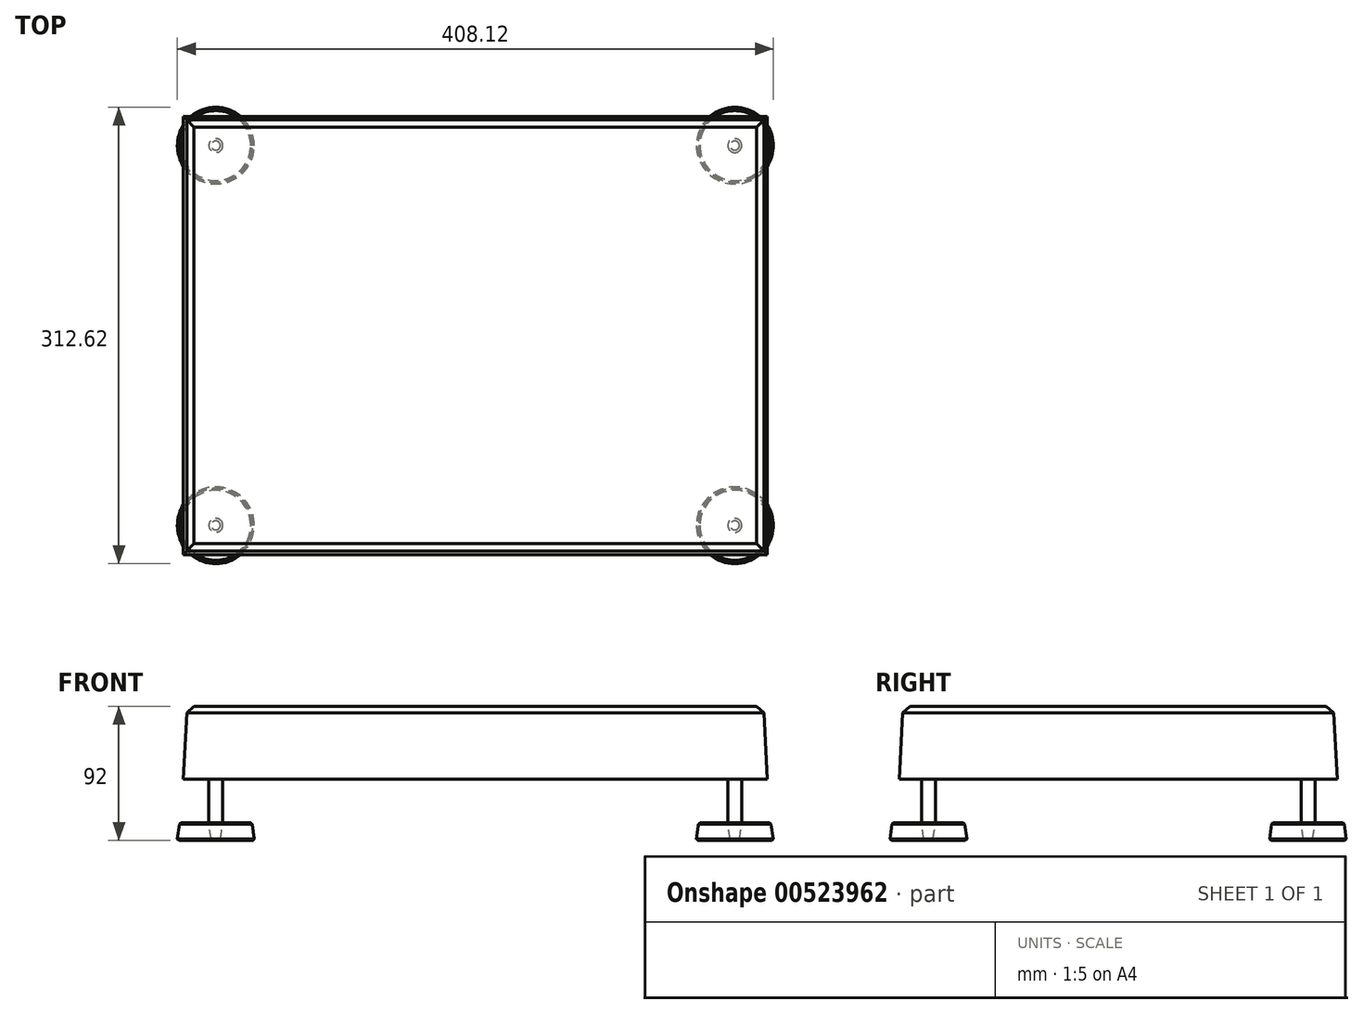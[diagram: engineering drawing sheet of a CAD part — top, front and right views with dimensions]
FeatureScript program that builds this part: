
annotation { "Feature Type Name" : "Feature", "Feature Type Description" : "" }
export const myFeature = defineFeature(function(context is Context, id is Id, definition is map)
    precondition{}
    {
        {
            var Q0;
            Q0=qCreatedBy(makeId("Top.planeOp"),FACE);
            var sketch = newSketch(context, id + "F0", { "sketchPlane" : qUnion([Q0])});
            skLineSegment(sketch, "E0.bottom", {"start": v(200, -150) * mm, "end": v(-200, -150) * mm});
            skLineSegment(sketch, "E0.top", {"start": v(200, 150) * mm, "end": v(-200, 150) * mm});
            skLineSegment(sketch, "E0.left", {"start": v(200, -150) * mm, "end": v(200, 150) * mm});
            skLineSegment(sketch, "E0.right", {"start": v(-200, -150) * mm, "end": v(-200, 150) * mm});
            skPoint(sketch, "E0.middle", {"position": v(0, 0) * mm});
            skSolve(sketch);
        }
        {
            var Q0;
            Q0=makeQuery(id+"F0.imprint","IMPRINT",FACE,{"disambiguationData":[TD([[makeQuery(id+"F0.imprint","IMPRINT",EDGE,{"derivedFrom":sQuery(id+"F0.wireOp",EDGE,"E0.bottom")}),-1.0]])]});
            extrude(context, id + "F1", {"entities" : qUnion([Q0]), "depth" : 50 * mm, "offsetDistance" : 25 * mm, "hasDraft" : true, "draftAngle" : 3 * degree, "draftPullDirection" : true});
        }
        {
            var Q0;
            Q0=makeQuery(id+"F1.opExtrude","CAP_EDGE",EDGE,{"disambiguationData":[OSD([sQuery(id+"F0.wireOp",EDGE,"E0.bottom")])],"isStart":false});
            var Q1;
            Q1=makeQuery(id+"F1.opExtrude","CAP_EDGE",EDGE,{"disambiguationData":[OSD([sQuery(id+"F0.wireOp",EDGE,"E0.right")])],"isStart":false});
            var Q2;
            Q2=makeQuery(id+"F1.opExtrude","CAP_EDGE",EDGE,{"disambiguationData":[OSD([sQuery(id+"F0.wireOp",EDGE,"E0.left")])],"isStart":false});
            var Q3;
            Q3=makeQuery(id+"F1.opExtrude","SWEPT_EDGE",EDGE,{"disambiguationData":[OSD([sQuery(id+"F0.wireOp",EDGE,"E0.bottom"),sQuery(id+"F0.wireOp",EDGE,"E0.left")])]});
            var Q4;
            Q4=makeQuery(id+"F1.opExtrude","CAP_EDGE",EDGE,{"disambiguationData":[OSD([sQuery(id+"F0.wireOp",EDGE,"E0.top")])],"isStart":false});
            var Q5;
            Q5=makeQuery(id+"F1.opExtrude","SWEPT_EDGE",EDGE,{"disambiguationData":[OSD([sQuery(id+"F0.wireOp",EDGE,"E0.top"),sQuery(id+"F0.wireOp",EDGE,"E0.right")])]});
            chamfer(context, id + "F2", {"entities" : qUnion([Q0, Q1, Q2, Q3, Q4, Q5]), "width" : 5 * mm, "tangentPropagation" : true});
        }
        {
            var Q0;
            Q0=makeQuery(id+"F1.opExtrude","CAP_FACE",FACE,{"disambiguationData":[OSD([sQuery(id+"F0.wireOp",EDGE,"E0.bottom"),sQuery(id+"F0.wireOp",EDGE,"E0.top"),sQuery(id+"F0.wireOp",EDGE,"E0.left"),sQuery(id+"F0.wireOp",EDGE,"E0.right")])],"isStart":true});
            var sketch = newSketch(context, id + "F3", { "sketchPlane" : qUnion([Q0])});
            skLineSegment(sketch, "E1", {"start": v(0, 0) * mm, "end": v(200, 0) * mm, "construction": true});
            skLineSegment(sketch, "E2", {"start": v(-2.63, 150) * mm, "end": v(0, 0) * mm, "construction": true});
            skCircle(sketch, "E3", {"center": v(177.75, 130) * mm, "radius": 4.79 * mm});
            skSolve(sketch);
        }
        {
            var Q0;
            Q0 = qSketchRegion(id + "F3", true);
            extrude(context, id + "F4", {"entities" : qUnion([Q0]), "depth" : 30 * mm, "offsetDistance" : 25 * mm});
        }
        {
            var Q0;
            Q0=makeQuery(id+"F4.opExtrude","CAP_FACE",FACE,{"disambiguationData":[OSD([sQuery(id+"F3.wireOp",EDGE,"E3")])],"isStart":false});
            var sketch = newSketch(context, id + "F5", { "sketchPlane" : qUnion([Q0])});
            skCircle(sketch, "E4.0.0", {"center": v(177.75, 130) * mm, "radius": 4.79 * mm});
            skCircle(sketch, "E5.0", {"center": v(177.75, 130) * mm, "radius": 24.79 * mm});
            skSolve(sketch);
        }
        {
            var Q0;
            Q0 = qSketchRegion(id + "F5", true);
            extrude(context, id + "F6", {"entities" : qUnion([Q0]), "depth" : 12 * mm, "offsetDistance" : 25 * mm, "hasDraft" : true, "draftAngle" : 8 * degree});
        }
        {
            var Q0;
            Q0=makeQuery(id+"F6.opExtrude","CAP_EDGE",EDGE,{"disambiguationData":[OSD([sQuery(id+"F5.wireOp",EDGE,"E5.0")])],"isStart":false});
            var Q1;
            Q1=makeQuery(id+"F6.opExtrude","CAP_EDGE",EDGE,{"disambiguationData":[OSD([sQuery(id+"F5.wireOp",EDGE,"E5.0")])],"isStart":true});
            chamfer(context, id + "F7", {"entities" : qUnion([Q0, Q1]), "width" : 1 * mm, "tangentPropagation" : true});
        }
        {
            var Q0;
            Q0=makeQuery(id+"F4.opExtrude","SWEPT_BODY",BODY,{"disambiguationData":[OSD([sQuery(id+"F3.wireOp",EDGE,"E3")])]});
            var Q1;
            Q1=makeQuery(id+"F6.opExtrude","SWEPT_BODY",BODY,{"disambiguationData":[OSD([sQuery(id+"F5.wireOp",EDGE,"E4.0.0"),sQuery(id+"F5.wireOp",EDGE,"E5.0")])]});
            var Q2;
            Q2=qCreatedBy(makeId("Front.planeOp"),FACE);
            mirror(context, id + "F8", {"operationType" : NewBodyOperationType.ADD, "entities" : qUnion([Q0, Q1]), "mirrorPlane" : qUnion([Q2])});
        }
        {
            var Q0;
            Q0=makeQuery(id+"F1.opExtrude","SWEPT_BODY",BODY,{"disambiguationData":[OSD([sQuery(id+"F0.wireOp",EDGE,"E0.bottom"),sQuery(id+"F0.wireOp",EDGE,"E0.top"),sQuery(id+"F0.wireOp",EDGE,"E0.left"),sQuery(id+"F0.wireOp",EDGE,"E0.right")])]});
            var Q1;
            Q1=makeQuery(id+"F8.boolean.opBoolean","MERGE",BODY,{"derivedFrom":[makeQuery(id+"F4.opExtrude","SWEPT_BODY",BODY,{"disambiguationData":[OSD([sQuery(id+"F3.wireOp",EDGE,"E3")])]}),makeQuery(id+"F6.opExtrude","SWEPT_BODY",BODY,{"disambiguationData":[OSD([sQuery(id+"F5.wireOp",EDGE,"E4.0.0"),sQuery(id+"F5.wireOp",EDGE,"E5.0")])]})]});
            var Q2;
            Q2=makeQuery(id+"F8.boolean.opBoolean","MERGE",BODY,{"derivedFrom":[makeQuery(id+"F8.opPattern","COPY",BODY,{"derivedFrom":makeQuery(id+"F4.opExtrude","SWEPT_BODY",BODY,{"disambiguationData":[OSD([sQuery(id+"F3.wireOp",EDGE,"E3")])]}),"instanceName":"1"}),makeQuery(id+"F8.opPattern","COPY",BODY,{"derivedFrom":makeQuery(id+"F6.opExtrude","SWEPT_BODY",BODY,{"disambiguationData":[OSD([sQuery(id+"F5.wireOp",EDGE,"E4.0.0"),sQuery(id+"F5.wireOp",EDGE,"E5.0")])]}),"instanceName":"1"})]});
            var Q3;
            Q3=qCreatedBy(makeId("Right.planeOp"),FACE);
            mirror(context, id + "F9", {"operationType" : NewBodyOperationType.ADD, "entities" : qUnion([Q0, Q1, Q2]), "mirrorPlane" : qUnion([Q3])});
        }
    });
